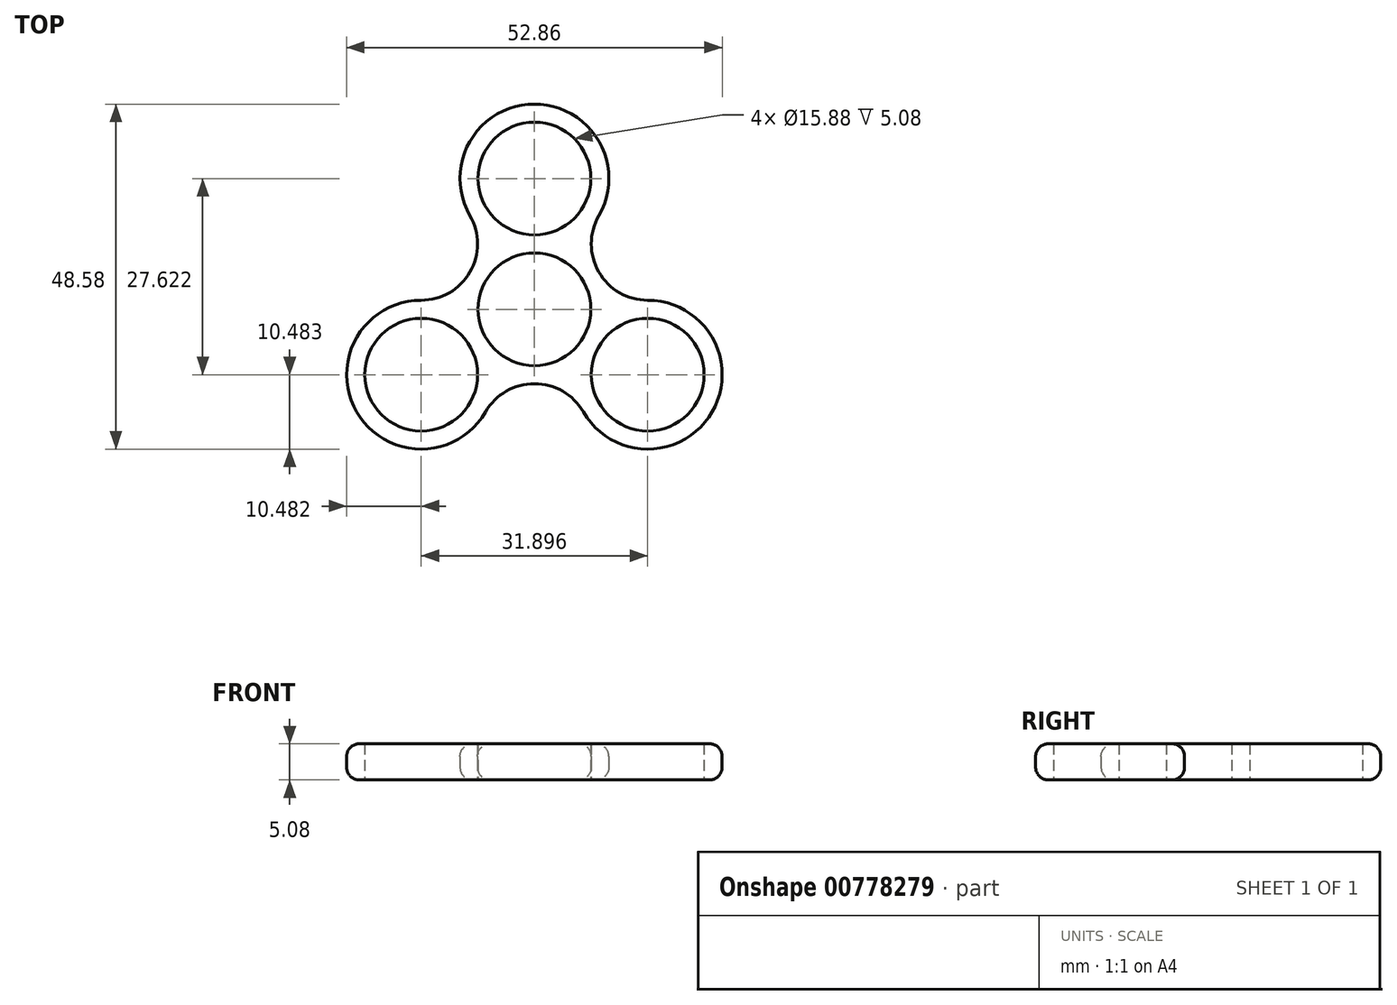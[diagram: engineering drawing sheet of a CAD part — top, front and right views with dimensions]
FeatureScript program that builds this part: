
annotation { "Feature Type Name" : "Feature", "Feature Type Description" : "" }
export const myFeature = defineFeature(function(context is Context, id is Id, definition is map)
    precondition{}
    {
        {
            var Q0;
            Q0=qCreatedBy(makeId("Top.planeOp"),FACE);
            var sketch = newSketch(context, id + "F0", { "sketchPlane" : qUnion([Q0])});
            skCircle(sketch, "E0", {"center": v(0, 0) * mm, "radius": 7.94 * mm});
            skCircle(sketch, "E1", {"center": v(0, 18.41) * mm, "radius": 7.94 * mm});
            skArc(sketch, "E2.0", {"start": v(9.07, 13.18) * mm, "mid": v(0, 28.9) * mm, "end": v(-9.07, 13.18) * mm});
            skArc(sketch, "E3.1.0", {"start": v(-15.95, 1.27) * mm, "mid": v(-25.02, -14.45) * mm, "end": v(-6.87, -14.45) * mm});
            skCircle(sketch, "E3.1.1", {"center": v(-15.95, -9.2) * mm, "radius": 7.94 * mm});
            skArc(sketch, "E3.2.0", {"start": v(6.87, -14.45) * mm, "mid": v(25.02, -14.45) * mm, "end": v(15.95, 1.27) * mm});
            skCircle(sketch, "E3.2.1", {"center": v(15.95, -9.2) * mm, "radius": 7.94 * mm});
            skArc(sketch, "E4", {"start": v(-15.95, 1.27) * mm, "mid": v(-9.07, 5.24) * mm, "end": v(-9.07, 13.18) * mm});
            skArc(sketch, "E5.1.0", {"start": v(6.87, -14.45) * mm, "mid": v(0, -10.48) * mm, "end": v(-6.87, -14.45) * mm});
            skArc(sketch, "E5.2.0", {"start": v(9.07, 13.18) * mm, "mid": v(9.07, 5.24) * mm, "end": v(15.95, 1.27) * mm});
            skSolve(sketch);
        }
        {
            var Q0;
            Q0 = qSketchRegion(id + "F0", true);
            extrude(context, id + "F1", {"entities" : qUnion([Q0]), "depth" : 5.08 * mm, "offsetDistance" : 25.4 * mm});
        }
        {
            var Q0;
            Q0=makeQuery(id+"F1.opExtrude","CAP_EDGE",EDGE,{"disambiguationData":[OSD([sQuery(id+"F0.wireOp",EDGE,"E4")])],"isStart":false});
            var Q1;
            Q1=makeQuery(id+"F1.opExtrude","CAP_EDGE",EDGE,{"disambiguationData":[OSD([sQuery(id+"F0.wireOp",EDGE,"E2.0")])],"isStart":true});
            fillet(context, id + "F2", {"entities" : qUnion([Q0, Q1]), "radius" : 1.78 * mm, "tangentPropagation" : true, "allowEdgeOverflow" : false});
        }
    });
